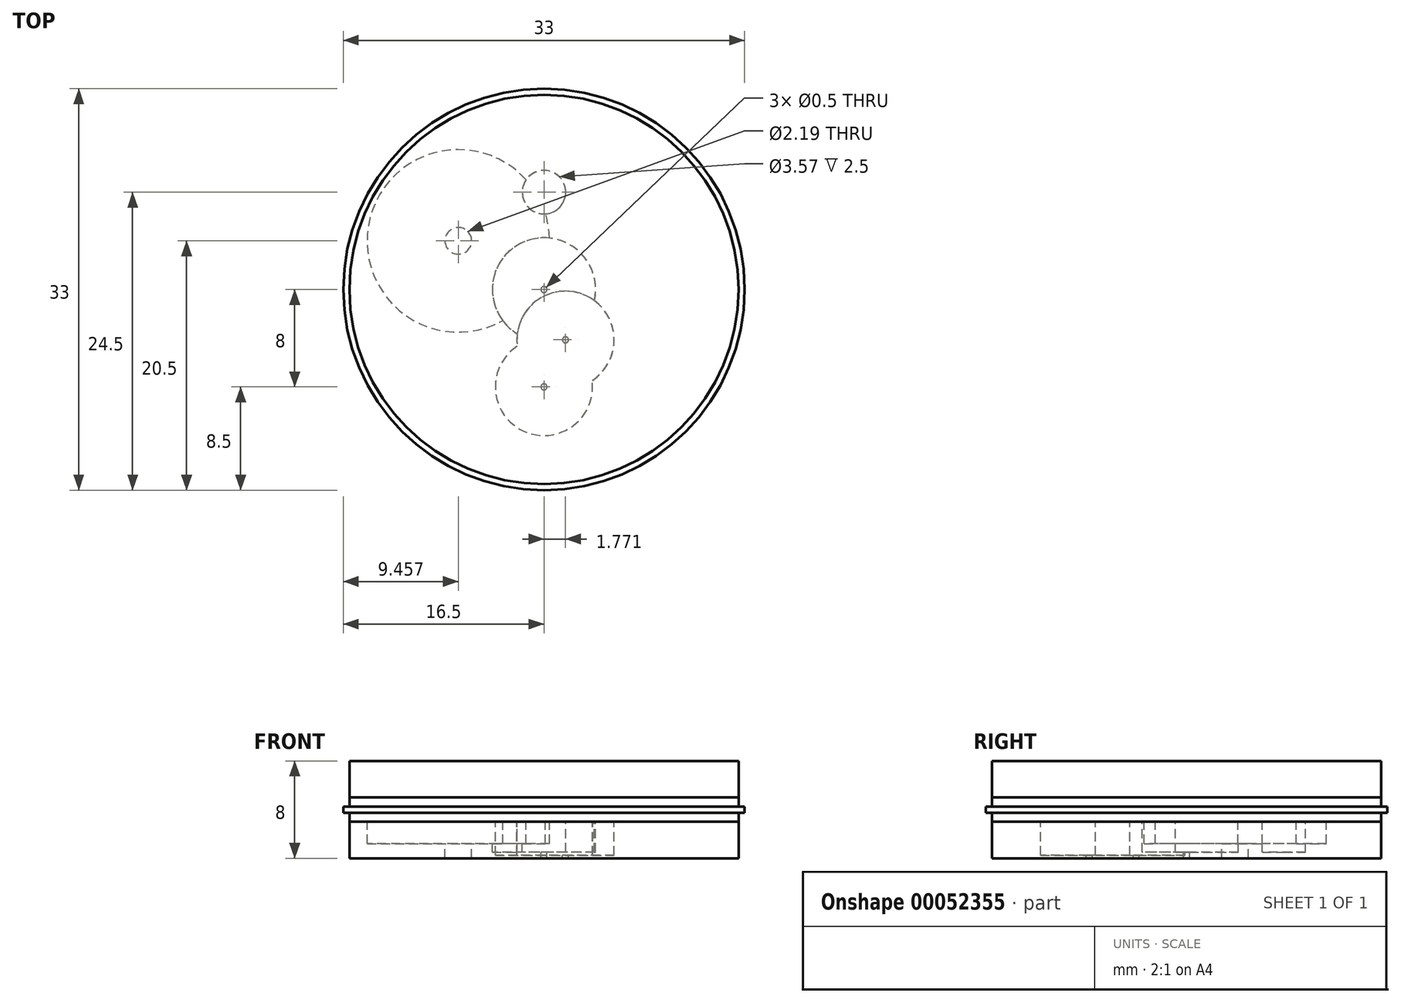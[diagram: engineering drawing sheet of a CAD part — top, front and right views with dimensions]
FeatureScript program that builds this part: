
annotation { "Feature Type Name" : "Feature", "Feature Type Description" : "" }
export const myFeature = defineFeature(function(context is Context, id is Id, definition is map)
    precondition{}
    {
        {
            var Q0;
            Q0=qCreatedBy(makeId("Top.planeOp"),FACE);
            var sketch = newSketch(context, id + "F0", { "sketchPlane" : qUnion([Q0])});
            skCircle(sketch, "E0", {"center": v(0, 0) * mm, "radius": 16 * mm});
            skCircle(sketch, "E1", {"center": v(0, 0) * mm, "radius": 16.5 * mm});
            skSolve(sketch);
        }
        {
            var Q0;
            Q0=makeQuery(id+"F0.imprint","IMPRINT",FACE,{"disambiguationData":[TD([[makeQuery(id+"F0.imprint","IMPRINT",EDGE,{"derivedFrom":sQuery(id+"F0.wireOp",EDGE,"E0")}),1.0]])]});
            extrude(context, id + "F1", {"entities" : qUnion([Q0]), "depth" : 2 * mm, "symmetric" : true});
        }
        {
            var Q0;
            Q0=makeQuery(id+"F0.imprint","IMPRINT",FACE,{"disambiguationData":[TD([[makeQuery(id+"F0.imprint","IMPRINT",EDGE,{"derivedFrom":sQuery(id+"F0.wireOp",EDGE,"E0")}),-1.0]])]});
            extrude(context, id + "F2", {"entities" : qUnion([Q0]), "operationType" : NewBodyOperationType.ADD, "depth" : 0.5 * mm, "symmetric" : true});
        }
        {
            var Q0;
            Q0=makeQuery(id+"F1.opExtrude","CAP_FACE",FACE,{"disambiguationData":[OSD([sQuery(id+"F0.wireOp",EDGE,"E0")])],"isStart":false});
            var sketch = newSketch(context, id + "F3", { "sketchPlane" : qUnion([Q0])});
            skCircle(sketch, "E2.0", {"center": v(0, 0) * mm, "radius": 16 * mm});
            skSolve(sketch);
        }
        {
            var Q0;
            Q0=qSketchRegion(id+"F3",true);
            extrude(context, id + "F4", {"entities" : qUnion([Q0]), "depth" : 3 * mm});
        }
        {
            var Q0;
            Q0=makeQuery(id+"F1.opExtrude","CAP_FACE",FACE,{"disambiguationData":[OSD([sQuery(id+"F0.wireOp",EDGE,"E0")])],"isStart":true});
            var sketch = newSketch(context, id + "F5", { "sketchPlane" : qUnion([Q0])});
            skCircle(sketch, "E3.0", {"center": v(0, 0) * mm, "radius": 16 * mm});
            skSolve(sketch);
        }
        {
            var Q0;
            Q0=qSketchRegion(id+"F5",true);
            extrude(context, id + "F6", {"entities" : qUnion([Q0]), "depth" : 3 * mm});
        }
        {
            var Q0;
            Q0=makeQuery(id+"F6.opExtrude","CAP_FACE",FACE,{"disambiguationData":[OSD([sQuery(id+"F5.wireOp",EDGE,"E3.0")])],"isStart":true});
            var sketch = newSketch(context, id + "F7", { "sketchPlane" : qUnion([Q0])});
            skCircle(sketch, "E4", {"center": v(0, 0) * mm, "radius": 0.25 * mm});
            skLineSegment(sketch, "E5", {"start": v(0, 0) * mm, "end": v(0, -8) * mm, "construction": true});
            skLineSegment(sketch, "E6", {"start": v(0, 0) * mm, "end": v(1.77, -4.14) * mm, "construction": true});
            skLineSegment(sketch, "E7", {"start": v(1.77, -4.14) * mm, "end": v(0, -8) * mm, "construction": true});
            skCircle(sketch, "E8", {"center": v(1.77, -4.14) * mm, "radius": 0.25 * mm});
            skCircle(sketch, "E9", {"center": v(1.77, -4.14) * mm, "radius": 4 * mm});
            skCircle(sketch, "E10", {"center": v(0, 0) * mm, "radius": 4.25 * mm});
            skLineSegment(sketch, "E11", {"start": v(0, 0) * mm, "end": v(0, 8) * mm, "construction": true});
            skLineSegment(sketch, "E12", {"start": v(0, 8) * mm, "end": v(-7.04, 4) * mm, "construction": true});
            skLineSegment(sketch, "E13", {"start": v(-7.04, 4) * mm, "end": v(0, 0) * mm, "construction": true});
            skCircle(sketch, "E14", {"center": v(0, 8) * mm, "radius": 1.79 * mm});
            skCircle(sketch, "E15", {"center": v(-7.04, 4) * mm, "radius": 1.1 * mm});
            skCircle(sketch, "E16", {"center": v(-7.04, 4) * mm, "radius": 7.5 * mm});
            skCircle(sketch, "E17", {"center": v(0, -8) * mm, "radius": 4 * mm});
            skCircle(sketch, "E18", {"center": v(0, -8) * mm, "radius": 0.25 * mm});
            skSolve(sketch);
        }
        {
            var Q0;
            Q0=makeQuery(id+"F7.imprint","IMPRINT",FACE,{"disambiguationData":[TD([[makeQuery(id+"F7.imprint","IMPRINT",EDGE,{"derivedFrom":sQuery(id+"F7.wireOp",EDGE,"E8")}),1.0]])]});
            extrude(context, id + "F8", {"entities" : qUnion([Q0]), "operationType" : NewBodyOperationType.REMOVE, "endBound" : BoundingType.THROUGH_ALL, "oppositeDirection" : true, "depth" : 25 * mm});
        }
        {
            var Q0;
            Q0=makeQuery(id+"F7.imprint","IMPRINT",FACE,{"disambiguationData":[TD([[makeQuery(id+"F7.imprint","IMPRINT",EDGE,{"derivedFrom":sQuery(id+"F7.wireOp",EDGE,"E8")}),-1.0]])]});
            var Q1;
            {var subQ0=sQuery(id+"F7.wireOp",EDGE,"E10");var subQ1=sQuery(id+"F7.wireOp",EDGE,"E9");var subQ2=makeQuery(id+"F7.imprint","INTERSECT",VERTEX,{"disambiguationData":[OD(0.0)],"derivedFrom":[subQ1,subQ0]});Q1=makeQuery(id+"F7.imprint","IMPRINT",FACE,{"disambiguationData":[TD([[makeQuery(id+"F7.imprint","IMPRINT",EDGE,{"disambiguationData":[TD([[subQ2,1.0]])],"derivedFrom":subQ1}),1.0]])]});}
            var Q2;
            {var subQ0=sQuery(id+"F7.wireOp",EDGE,"E10");var subQ1=sQuery(id+"F7.wireOp",EDGE,"E8");var subQ2=makeQuery(id+"F7.imprint","INTERSECT",VERTEX,{"derivedFrom":[subQ1,subQ0]});Q2=makeQuery(id+"F7.imprint","IMPRINT",FACE,{"disambiguationData":[TD([[makeQuery(id+"F7.imprint","IMPRINT",EDGE,{"disambiguationData":[TD([[subQ2,1.0]])],"derivedFrom":subQ1}),-1.0]])]});}
            var Q3;
            {var subQ0=sQuery(id+"F7.wireOp",EDGE,"E17");var subQ5=sQuery(id+"F7.wireOp",EDGE,"E9");var subQ7=makeQuery(id+"F7.imprint","INTERSECT",VERTEX,{"disambiguationData":[OD(0.0)],"derivedFrom":[subQ5,subQ0]});Q3=makeQuery(id+"F7.imprint","IMPRINT",FACE,{"disambiguationData":[TD([[makeQuery(id+"F7.imprint","IMPRINT",EDGE,{"disambiguationData":[TD([[subQ7,-1.0]])],"derivedFrom":subQ5}),1.0]])]});}
            var Q4;
            {var subQ0=sQuery(id+"F7.wireOp",EDGE,"E10");var subQ1=sQuery(id+"F7.wireOp",EDGE,"E9");var subQ2=makeQuery(id+"F7.imprint","INTERSECT",VERTEX,{"disambiguationData":[OD(0.0)],"derivedFrom":[subQ1,subQ0]});Q4=makeQuery(id+"F7.imprint","IMPRINT",FACE,{"disambiguationData":[TD([[makeQuery(id+"F7.imprint","IMPRINT",EDGE,{"disambiguationData":[TD([[subQ2,-1.0]])],"derivedFrom":subQ1}),1.0]])]});}
            var Q5;
            {var subQ0=sQuery(id+"F7.wireOp",EDGE,"E17");var subQ1=sQuery(id+"F7.wireOp",EDGE,"E10");var subQ2=makeQuery(id+"F7.imprint","INTERSECT",VERTEX,{"disambiguationData":[OD(0.0)],"derivedFrom":[subQ1,subQ0]});Q5=makeQuery(id+"F7.imprint","IMPRINT",FACE,{"disambiguationData":[TD([[makeQuery(id+"F7.imprint","IMPRINT",EDGE,{"disambiguationData":[TD([[subQ2,-1.0]])],"derivedFrom":subQ1}),1.0]])]});}
            extrude(context, id + "F9", {"entities" : qUnion([Q0, Q1, Q2, Q3, Q4, Q5]), "operationType" : NewBodyOperationType.REMOVE, "oppositeDirection" : true, "depth" : 2.75 * mm});
        }
        {
            var Q0;
            Q0=makeQuery(id+"F7.imprint","IMPRINT",FACE,{"disambiguationData":[TD([[makeQuery(id+"F7.imprint","IMPRINT",EDGE,{"derivedFrom":sQuery(id+"F7.wireOp",EDGE,"E4")}),1.0]])]});
            extrude(context, id + "F10", {"entities" : qUnion([Q0]), "operationType" : NewBodyOperationType.REMOVE, "endBound" : BoundingType.THROUGH_ALL, "oppositeDirection" : true, "depth" : 25 * mm});
        }
        {
            var Q0;
            Q0=makeQuery(id+"F7.imprint","IMPRINT",FACE,{"disambiguationData":[TD([[makeQuery(id+"F7.imprint","IMPRINT",EDGE,{"derivedFrom":sQuery(id+"F7.wireOp",EDGE,"E4")}),-1.0]])]});
            var Q1;
            {var subQ0=sQuery(id+"F7.wireOp",EDGE,"E16");var subQ1=sQuery(id+"F7.wireOp",EDGE,"E10");var subQ2=makeQuery(id+"F7.imprint","INTERSECT",VERTEX,{"disambiguationData":[OD(0.0)],"derivedFrom":[subQ1,subQ0]});Q1=makeQuery(id+"F7.imprint","IMPRINT",FACE,{"disambiguationData":[TD([[makeQuery(id+"F7.imprint","IMPRINT",EDGE,{"disambiguationData":[TD([[subQ2,1.0]])],"derivedFrom":subQ1}),1.0]])]});}
            extrude(context, id + "F11", {"entities" : qUnion([Q0, Q1]), "operationType" : NewBodyOperationType.REMOVE, "oppositeDirection" : true, "depth" : 2.5 * mm});
        }
        {
            var Q0;
            Q0=makeQuery(id+"F7.imprint","IMPRINT",FACE,{"disambiguationData":[TD([[makeQuery(id+"F7.imprint","IMPRINT",EDGE,{"derivedFrom":sQuery(id+"F7.wireOp",EDGE,"E15")}),1.0]])]});
            extrude(context, id + "F12", {"entities" : qUnion([Q0]), "operationType" : NewBodyOperationType.REMOVE, "endBound" : BoundingType.THROUGH_ALL, "oppositeDirection" : true, "depth" : 25 * mm});
        }
        {
            var Q0;
            Q0=makeQuery(id+"F7.imprint","IMPRINT",FACE,{"disambiguationData":[TD([[makeQuery(id+"F7.imprint","IMPRINT",EDGE,{"derivedFrom":sQuery(id+"F7.wireOp",EDGE,"E15")}),-1.0]])]});
            var Q1;
            {var subQ0=sQuery(id+"F7.wireOp",EDGE,"E16");var subQ1=sQuery(id+"F7.wireOp",EDGE,"E14");var subQ2=makeQuery(id+"F7.imprint","INTERSECT",VERTEX,{"disambiguationData":[OD(0.0)],"derivedFrom":[subQ1,subQ0]});Q1=makeQuery(id+"F7.imprint","IMPRINT",FACE,{"disambiguationData":[TD([[makeQuery(id+"F7.imprint","IMPRINT",EDGE,{"disambiguationData":[TD([[subQ2,1.0]])],"derivedFrom":subQ1}),1.0]])]});}
            extrude(context, id + "F13", {"entities" : qUnion([Q0, Q1]), "operationType" : NewBodyOperationType.REMOVE, "oppositeDirection" : true, "depth" : 1.8 * mm});
        }
        {
            var Q0;
            {var subQ0=sQuery(id+"F7.wireOp",EDGE,"E17");var subQ1=sQuery(id+"F7.wireOp",EDGE,"E9");var subQ2=makeQuery(id+"F7.imprint","INTERSECT",VERTEX,{"disambiguationData":[OD(0.0)],"derivedFrom":[subQ1,subQ0]});Q0=makeQuery(id+"F7.imprint","IMPRINT",FACE,{"disambiguationData":[TD([[makeQuery(id+"F7.imprint","IMPRINT",EDGE,{"disambiguationData":[TD([[subQ2,-1.0]])],"derivedFrom":subQ1}),-1.0]])]});}
            var Q1;
            {var subQ0=sQuery(id+"F7.wireOp",EDGE,"E17");var subQ5=sQuery(id+"F7.wireOp",EDGE,"E9");var subQ7=makeQuery(id+"F7.imprint","INTERSECT",VERTEX,{"disambiguationData":[OD(0.0)],"derivedFrom":[subQ5,subQ0]});Q1=makeQuery(id+"F7.imprint","IMPRINT",FACE,{"disambiguationData":[TD([[makeQuery(id+"F7.imprint","IMPRINT",EDGE,{"disambiguationData":[TD([[subQ7,-1.0]])],"derivedFrom":subQ5}),1.0]])]});}
            var Q2;
            {var subQ0=sQuery(id+"F7.wireOp",EDGE,"E17");var subQ1=sQuery(id+"F7.wireOp",EDGE,"E10");var subQ2=makeQuery(id+"F7.imprint","INTERSECT",VERTEX,{"disambiguationData":[OD(0.0)],"derivedFrom":[subQ1,subQ0]});Q2=makeQuery(id+"F7.imprint","IMPRINT",FACE,{"disambiguationData":[TD([[makeQuery(id+"F7.imprint","IMPRINT",EDGE,{"disambiguationData":[TD([[subQ2,-1.0]])],"derivedFrom":subQ1}),1.0]])]});}
            var Q3;
            Q3=makeQuery(id+"F9.boolean.opBoolean","COPY",FACE,{"derivedFrom":makeQuery(id+"F9.opExtrude","CAP_FACE",FACE,{"disambiguationData":[OSD([sQuery(id+"F7.wireOp",EDGE,"E8"),sQuery(id+"F7.wireOp",EDGE,"E9")])],"isStart":false})});
            extrude(context, id + "F14", {"entities" : qUnion([Q0, Q1, Q2]), "operationType" : NewBodyOperationType.REMOVE, "endBound" : BoundingType.UP_TO_SURFACE, "oppositeDirection" : true, "endBoundEntityFace" : qUnion([Q3]), "depth" : 2 * mm});
        }
        {
            var Q0;
            Q0=makeQuery(id+"F7.imprint","IMPRINT",FACE,{"disambiguationData":[TD([[makeQuery(id+"F7.imprint","IMPRINT",EDGE,{"derivedFrom":sQuery(id+"F7.wireOp",EDGE,"E18")}),1.0]])]});
            extrude(context, id + "F15", {"entities" : qUnion([Q0]), "operationType" : NewBodyOperationType.REMOVE, "endBound" : BoundingType.THROUGH_ALL, "oppositeDirection" : true, "depth" : 25 * mm});
        }
        {
            var Q0;
            {var subQ0=sQuery(id+"F7.wireOp",EDGE,"E16");var subQ1=sQuery(id+"F7.wireOp",EDGE,"E14");var subQ2=makeQuery(id+"F7.imprint","INTERSECT",VERTEX,{"disambiguationData":[OD(0.0)],"derivedFrom":[subQ1,subQ0]});Q0=makeQuery(id+"F7.imprint","IMPRINT",FACE,{"disambiguationData":[TD([[makeQuery(id+"F7.imprint","IMPRINT",EDGE,{"disambiguationData":[TD([[subQ2,-1.0]])],"derivedFrom":subQ1}),1.0]])]});}
            var Q1;
            {var subQ0=sQuery(id+"F7.wireOp",EDGE,"E16");var subQ1=sQuery(id+"F7.wireOp",EDGE,"E14");var subQ2=makeQuery(id+"F7.imprint","INTERSECT",VERTEX,{"disambiguationData":[OD(0.0)],"derivedFrom":[subQ1,subQ0]});Q1=makeQuery(id+"F7.imprint","IMPRINT",FACE,{"disambiguationData":[TD([[makeQuery(id+"F7.imprint","IMPRINT",EDGE,{"disambiguationData":[TD([[subQ2,1.0]])],"derivedFrom":subQ1}),1.0]])]});}
            var Q2;
            Q2=makeQuery(id+"F11.boolean.opBoolean","COPY",FACE,{"derivedFrom":makeQuery(id+"F11.opExtrude","CAP_FACE",FACE,{"disambiguationData":[OSD([sQuery(id+"F7.wireOp",EDGE,"E4"),sQuery(id+"F7.wireOp",EDGE,"E9"),sQuery(id+"F7.wireOp",EDGE,"E10")])],"isStart":false})});
            extrude(context, id + "F16", {"entities" : qUnion([Q0, Q1]), "operationType" : NewBodyOperationType.REMOVE, "endBound" : BoundingType.UP_TO_SURFACE, "oppositeDirection" : true, "endBoundEntityFace" : qUnion([Q2]), "depth" : 25 * mm});
        }
    });
